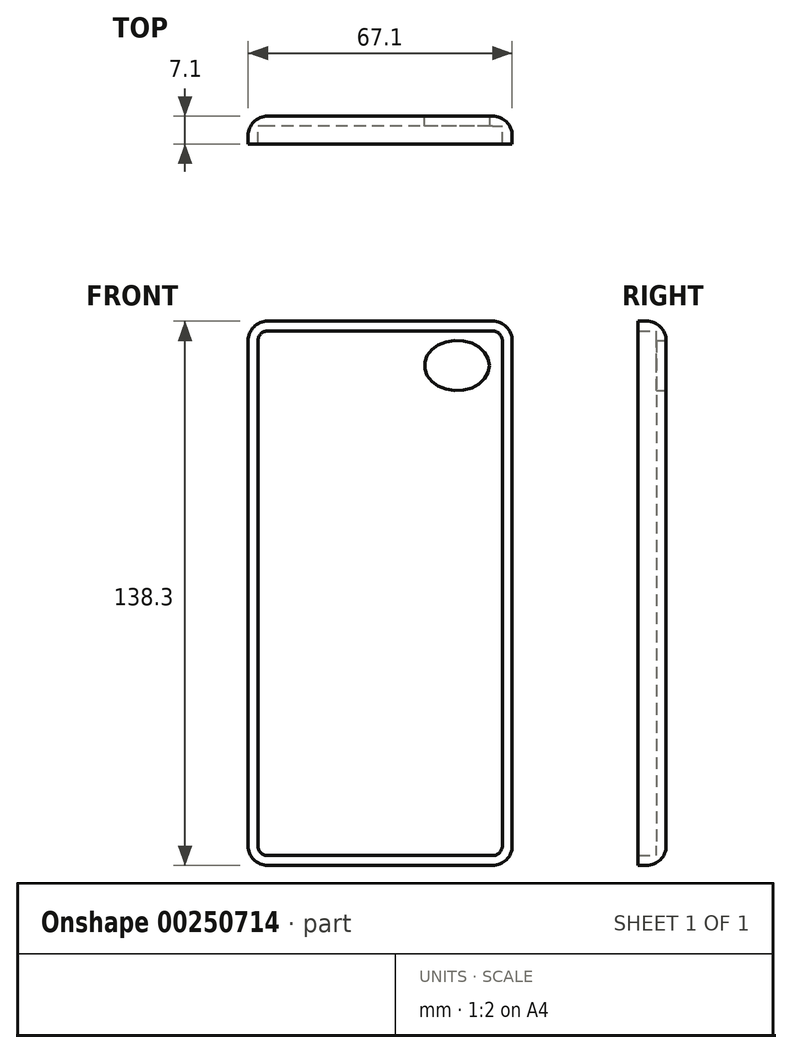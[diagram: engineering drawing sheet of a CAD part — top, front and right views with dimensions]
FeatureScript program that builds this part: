
annotation { "Feature Type Name" : "Feature", "Feature Type Description" : "" }
export const myFeature = defineFeature(function(context is Context, id is Id, definition is map)
    precondition{}
    {
        {
            var Q0;
            Q0=qCreatedBy(makeId("Front.planeOp"),FACE);
            var sketch = newSketch(context, id + "F0", { "sketchPlane" : qUnion([Q0])});
            skLineSegment(sketch, "E0.bottom", {"start": v(33.55, 64.5) * mm, "end": v(-33.55, 64.5) * mm});
            skLineSegment(sketch, "E0.top", {"start": v(33.55, -73.8) * mm, "end": v(-33.55, -73.8) * mm});
            skLineSegment(sketch, "E0.left", {"start": v(33.55, 64.5) * mm, "end": v(33.55, -73.8) * mm});
            skLineSegment(sketch, "E0.right", {"start": v(-33.55, 64.5) * mm, "end": v(-33.55, -73.8) * mm});
            skPoint(sketch, "E0.middle", {"position": v(0, -4.65) * mm});
            skSolve(sketch);
        }
        {
            var Q0;
            Q0 = qSketchRegion(id + "F0", true);
            extrude(context, id + "F1", {"entities" : qUnion([Q0]), "endBound" : BoundingType.SYMMETRIC, "depth" : 7.1 * mm});
        }
        {
            var Q0;
            Q0=makeQuery(id+"F1.opExtrude","SWEPT_EDGE",EDGE,{"disambiguationData":[OSD([sQuery(id+"F0.wireOp",EDGE,"E0.bottom"),sQuery(id+"F0.wireOp",EDGE,"E0.right")])]});
            var Q1;
            Q1=makeQuery(id+"F1.opExtrude","SWEPT_EDGE",EDGE,{"disambiguationData":[OSD([sQuery(id+"F0.wireOp",EDGE,"E0.bottom"),sQuery(id+"F0.wireOp",EDGE,"E0.left")])]});
            var Q2;
            Q2=makeQuery(id+"F1.opExtrude","SWEPT_EDGE",EDGE,{"disambiguationData":[OSD([sQuery(id+"F0.wireOp",EDGE,"E0.top"),sQuery(id+"F0.wireOp",EDGE,"E0.left")])]});
            var Q3;
            Q3=makeQuery(id+"F1.opExtrude","SWEPT_EDGE",EDGE,{"disambiguationData":[OSD([sQuery(id+"F0.wireOp",EDGE,"E0.top"),sQuery(id+"F0.wireOp",EDGE,"E0.right")])]});
            fillet(context, id + "F2", {"entities" : qUnion([Q0, Q1, Q2, Q3]), "radius" : 5 * mm, "tangentPropagation" : true, "allowEdgeOverflow" : false});
        }
        {
            var Q0;
            Q0=makeQuery(id+"F1.opExtrude","CAP_FACE",FACE,{"disambiguationData":[OSD([sQuery(id+"F0.wireOp",EDGE,"E0.bottom"),sQuery(id+"F0.wireOp",EDGE,"E0.top"),sQuery(id+"F0.wireOp",EDGE,"E0.left"),sQuery(id+"F0.wireOp",EDGE,"E0.right")])],"isStart":false});
            shell(context, id + "F3", {"entities" : qUnion([Q0]), "thickness" : 2.5 * mm});
        }
        {
            var Q0;
            Q0=makeQuery(id+"F1.opExtrude","CAP_FACE",FACE,{"disambiguationData":[OSD([sQuery(id+"F0.wireOp",EDGE,"E0.bottom"),sQuery(id+"F0.wireOp",EDGE,"E0.top"),sQuery(id+"F0.wireOp",EDGE,"E0.left"),sQuery(id+"F0.wireOp",EDGE,"E0.right")])],"isStart":true});
            fillet(context, id + "F4", {"entities" : qUnion([Q0]), "radius" : 5 * mm, "tangentPropagation" : true, "allowEdgeOverflow" : false});
        }
        {
            var Q0;
            Q0=qCreatedBy(makeId("Front.planeOp"),FACE);
            var sketch = newSketch(context, id + "F5", { "sketchPlane" : qUnion([Q0])});
            skEllipse(sketch, "E1", {"center": v(19.5, 53.22) * mm, "majorRadius": 8.25 * mm, "minorRadius": 6.38 * mm, "majorAxis": v(1, 0)});
            skLineSegment(sketch, "E2.bottom", {"start": v(-8.01, 271.17) * mm, "end": v(8.86, 271.17) * mm});
            skLineSegment(sketch, "E2.top", {"start": v(-8.01, -381.17) * mm, "end": v(8.86, -381.17) * mm});
            skLineSegment(sketch, "E2.left", {"start": v(-8.01, 271.17) * mm, "end": v(-8.01, -381.17) * mm});
            skLineSegment(sketch, "E2.right", {"start": v(8.86, 271.17) * mm, "end": v(8.86, -381.17) * mm});
            skSolve(sketch);
        }
        {
            var Q0;
            Q0=makeQuery(id+"F5.imprint","IMPRINT",FACE,{"disambiguationData":[TD([[makeQuery(id+"F5.imprint","IMPRINT",EDGE,{"derivedFrom":sQuery(id+"F5.wireOp",EDGE,"E1")}),1.0]])]});
            extrude(context, id + "F6", {"entities" : qUnion([Q0]), "operationType" : NewBodyOperationType.REMOVE, "oppositeDirection" : true, "depth" : 25 * mm});
        }
    });
